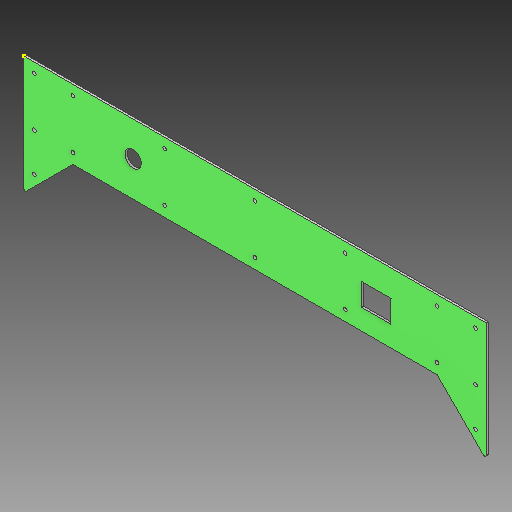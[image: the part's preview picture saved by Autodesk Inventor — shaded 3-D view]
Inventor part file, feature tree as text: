
AUTODESK INVENTOR PART (.ipt)
format: ipt  version: 2018 (Build 220112000, 112)  size: 821,248 bytes
history: native  units: mm
features: sketch x6, extrude x3, hole x1, projected_geometry x1
ambient origin geometry x8: Origin, YZ Plane, XZ Plane, XY Plane, X Axis, Y Axis, Z Axis, Center Point
bodies: Solid1 (feature_tree)
feature tree (11):
  extrude  "Extrusion1"  Depth=3.0mm TaperAngle=0.0deg
  sketch  "Sketch2"  dims[d6=5.0mm d7=6.0mm d8=4.0mm d9=2.0mm d10=90.0deg d11=8.0mm d12=20.594885mm d13=23.2mm]
  extrude  "Extrusion2"  Depth=23.2mm
  sketch  "Sketch5"
  hole  "Hole1"  [1 undecoded]
  extrude  "Extrusion3"  [1 undecoded]
  sketch  "Sketch8"
  sketch  "Sketch1"  dims[d0=3.0mm d1=0.0mm d4=194.0mm d5=0.0mm]
  projected_geometry  "Projected Loop1"
  sketch  "Sketch4"  dims[d14=10.0mm d15=0.0mm]
  sketch  "Sketch7"
note: 2 required parameter values undecoded (feature->parameter linkage not recoverable at this tier; creation-order binding heuristic only, values carry confidence <= 0.55)
